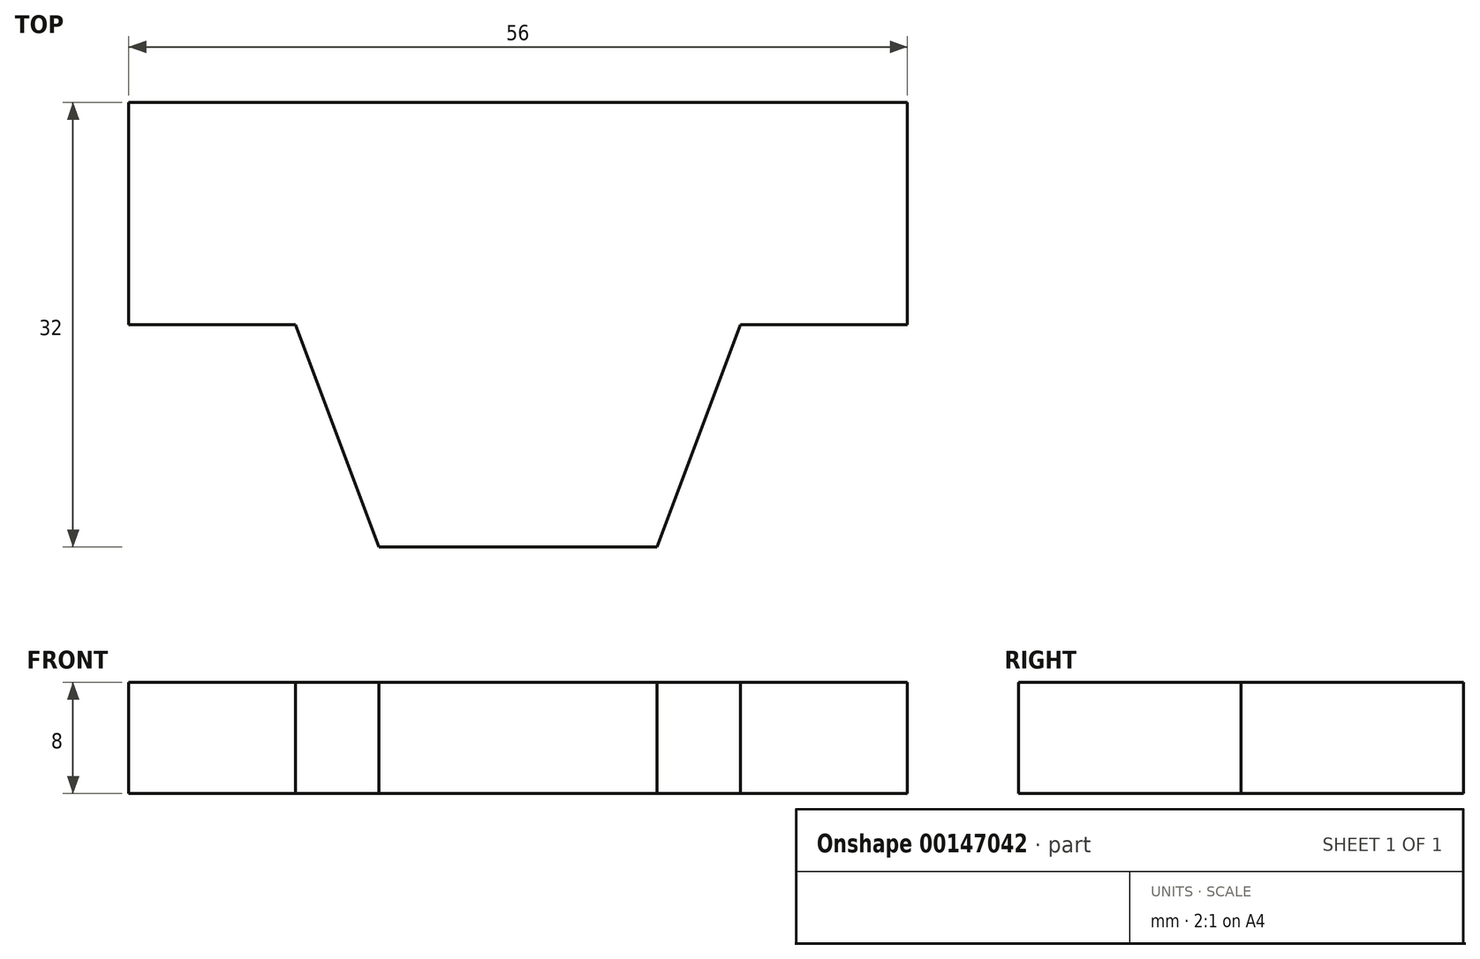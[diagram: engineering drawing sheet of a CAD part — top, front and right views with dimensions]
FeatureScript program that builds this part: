
annotation { "Feature Type Name" : "Feature", "Feature Type Description" : "" }
export const myFeature = defineFeature(function(context is Context, id is Id, definition is map)
    precondition{}
    {
        {
            var Q0;
            Q0=qCreatedBy(makeId("Top.planeOp"),FACE);
            var sketch = newSketch(context, id + "F0", { "sketchPlane" : qUnion([Q0])});
            skLineSegment(sketch, "E0", {"start": v(-33.37, 41.38) * mm, "end": v(22.63, 41.38) * mm});
            skLineSegment(sketch, "E1", {"start": v(22.63, 41.38) * mm, "end": v(22.63, 25.38) * mm});
            skLineSegment(sketch, "E2", {"start": v(22.63, 25.38) * mm, "end": v(10.63, 25.38) * mm});
            skLineSegment(sketch, "E3", {"start": v(-33.37, 41.38) * mm, "end": v(-33.37, 25.38) * mm});
            skLineSegment(sketch, "E4", {"start": v(-33.37, 25.38) * mm, "end": v(-21.37, 25.38) * mm});
            skLineSegment(sketch, "E5", {"start": v(-5.37, 41.38) * mm, "end": v(-5.37, 5.53) * mm, "construction": true});
            skLineSegment(sketch, "E6", {"start": v(-15.37, 9.38) * mm, "end": v(4.63, 9.38) * mm});
            skLineSegment(sketch, "E7", {"start": v(-21.37, 25.38) * mm, "end": v(-15.37, 9.38) * mm});
            skLineSegment(sketch, "E8", {"start": v(10.63, 25.38) * mm, "end": v(4.63, 9.38) * mm});
            skSolve(sketch);
        }
        {
            var Q0;
            Q0=makeQuery(id+"F0.imprint","IMPRINT",FACE,{"disambiguationData":[TD([[makeQuery(id+"F0.imprint","IMPRINT",EDGE,{"derivedFrom":sQuery(id+"F0.wireOp",EDGE,"E0")}),-1.0]])]});
            extrude(context, id + "F1", {"entities" : qUnion([Q0]), "depth" : 8 * mm});
        }
    });
